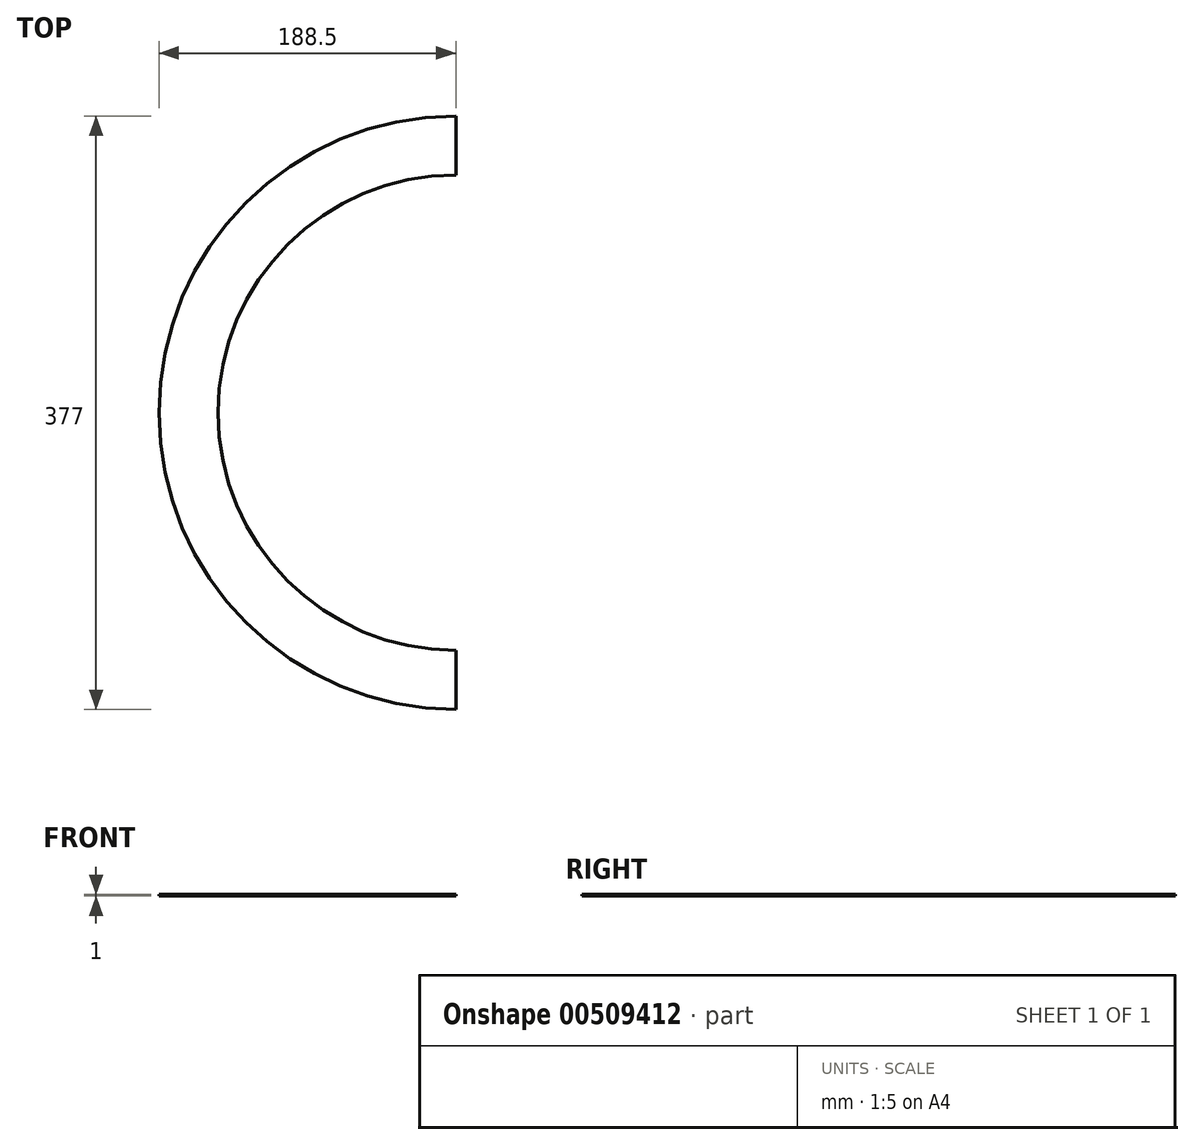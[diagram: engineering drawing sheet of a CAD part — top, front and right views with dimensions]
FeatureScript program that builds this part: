
annotation { "Feature Type Name" : "Feature", "Feature Type Description" : "" }
export const myFeature = defineFeature(function(context is Context, id is Id, definition is map)
    precondition{}
    {
        {
            var Q0;
            Q0=qCreatedBy(makeId("Top.planeOp"),FACE);
            var sketch = newSketch(context, id + "F0", { "sketchPlane" : qUnion([Q0])});
            skArc(sketch, "E0", {"start": v(0, 188.5) * mm, "mid": v(-188.5, 0) * mm, "end": v(0, -188.5) * mm});
            skArc(sketch, "E1", {"start": v(0, 151) * mm, "mid": v(-151, 0) * mm, "end": v(0, -151) * mm});
            skLineSegment(sketch, "E2", {"start": v(0, -188.5) * mm, "end": v(0, -151) * mm});
            skLineSegment(sketch, "E3.trimOffspring", {"start": v(0, 151) * mm, "end": v(0, 188.5) * mm});
            skSolve(sketch);
        }
        {
            var Q0;
            Q0=makeQuery(id+"F0.imprint","IMPRINT",FACE,{"disambiguationData":[TD([[makeQuery(id+"F0.imprint","IMPRINT",EDGE,{"derivedFrom":sQuery(id+"F0.wireOp",EDGE,"E0")}),1.0]])]});
            extrude(context, id + "F1", {"entities" : qUnion([Q0]), "oppositeDirection" : true, "depth" : 1 * mm});
        }
    });
